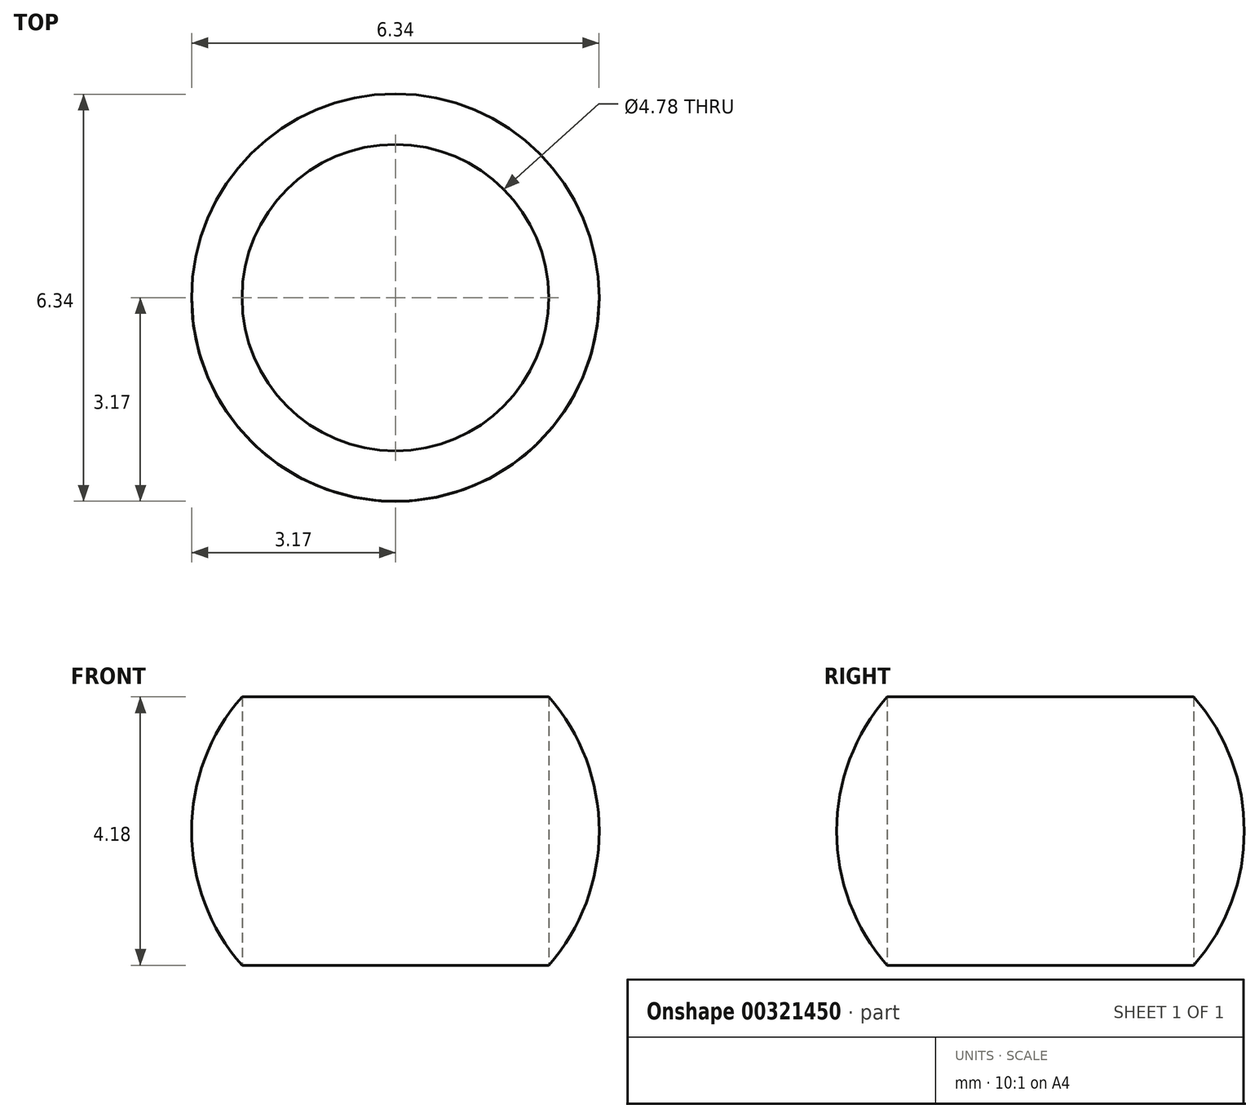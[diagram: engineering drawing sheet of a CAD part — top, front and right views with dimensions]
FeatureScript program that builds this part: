
annotation { "Feature Type Name" : "Feature", "Feature Type Description" : "" }
export const myFeature = defineFeature(function(context is Context, id is Id, definition is map)
    precondition{}
    {
        {
            var Q0;
            Q0=qCreatedBy(makeId("Front.planeOp"),FACE);
            var sketch = newSketch(context, id + "F0", { "sketchPlane" : qUnion([Q0])});
            skArc(sketch, "E0", {"start": v(3.18, 0) * mm, "mid": v(0, 3.18) * mm, "end": v(-3.18, 0) * mm});
            skLineSegment(sketch, "E1", {"start": v(-3.18, 0) * mm, "end": v(3.18, 0) * mm});
            skSolve(sketch);
        }
        {
            var Q0;
            Q0 = qSketchRegion(id + "F0", true);
            var Q1;
            Q1=sQuery(id+"F0.wireOp",EDGE,"E1");
            revolve(context, id + "F1", {"entities" : qUnion([Q0]), "axis" : qUnion([Q1]), "revolveType" : RevolveType.FULL});
        }
        {
            var Q0;
            Q0=qCreatedBy(makeId("Top.planeOp"),FACE);
            var sketch = newSketch(context, id + "F2", { "sketchPlane" : qUnion([Q0])});
            skCircle(sketch, "E2", {"center": v(0, 0) * mm, "radius": 2.39 * mm});
            skSolve(sketch);
        }
        {
            var Q0;
            Q0 = qSketchRegion(id + "F2", true);
            extrude(context, id + "F3", {"entities" : qUnion([Q0]), "operationType" : NewBodyOperationType.REMOVE, "endBound" : BoundingType.THROUGH_ALL, "depth" : 25 * mm, "hasSecondDirection" : true, "secondDirectionBound" : SecondDirectionBoundingType.THROUGH_ALL, "secondDirectionOppositeDirection" : true, "secondDirectionDepth" : 25 * mm});
        }
    });
